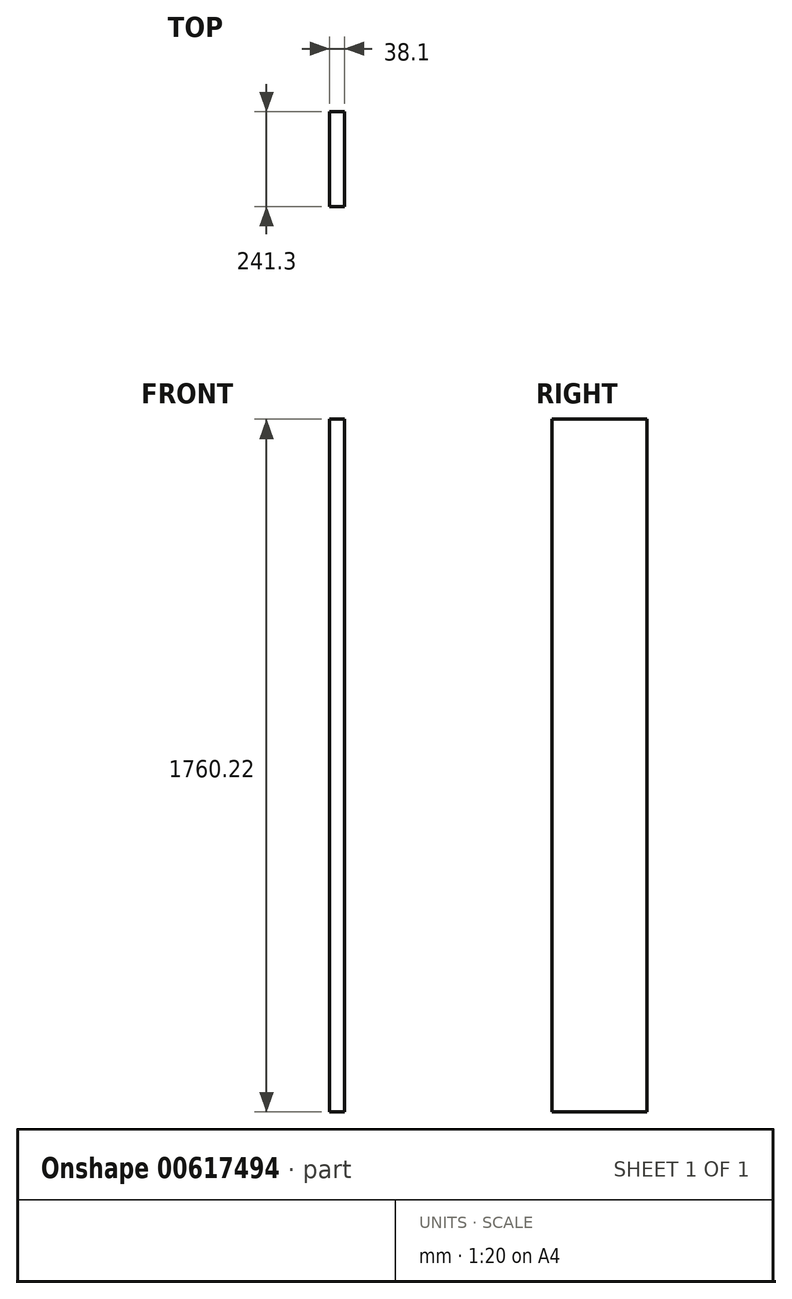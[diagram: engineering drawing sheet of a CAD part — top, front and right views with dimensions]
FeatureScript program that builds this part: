
annotation { "Feature Type Name" : "Feature", "Feature Type Description" : "" }
export const myFeature = defineFeature(function(context is Context, id is Id, definition is map)
    precondition{}
    {
        {
            var Q0;
            Q0=qCreatedBy(makeId("Top.planeOp"),FACE);
            var sketch = newSketch(context, id + "F0", { "sketchPlane" : qUnion([Q0])});
            skLineSegment(sketch, "E0.bottom", {"start": v(0, 0) * mm, "end": v(38.1, 0) * mm});
            skLineSegment(sketch, "E0.top", {"start": v(0, 241.3) * mm, "end": v(38.1, 241.3) * mm});
            skLineSegment(sketch, "E0.left", {"start": v(0, 0) * mm, "end": v(0, 241.3) * mm});
            skLineSegment(sketch, "E0.right", {"start": v(38.1, 0) * mm, "end": v(38.1, 241.3) * mm});
            skSolve(sketch);
        }
        {
            var Q0;
            Q0=makeQuery(id+"F0.imprint","IMPRINT",FACE,{"disambiguationData":[TD([[makeQuery(id+"F0.imprint","IMPRINT",EDGE,{"derivedFrom":sQuery(id+"F0.wireOp",EDGE,"E0.bottom")}),1.0]])]});
            extrude(context, id + "F1", {"entities" : qUnion([Q0]), "depth" : 1760.22 * mm, "offsetDistance" : 25.4 * mm});
        }
    });
